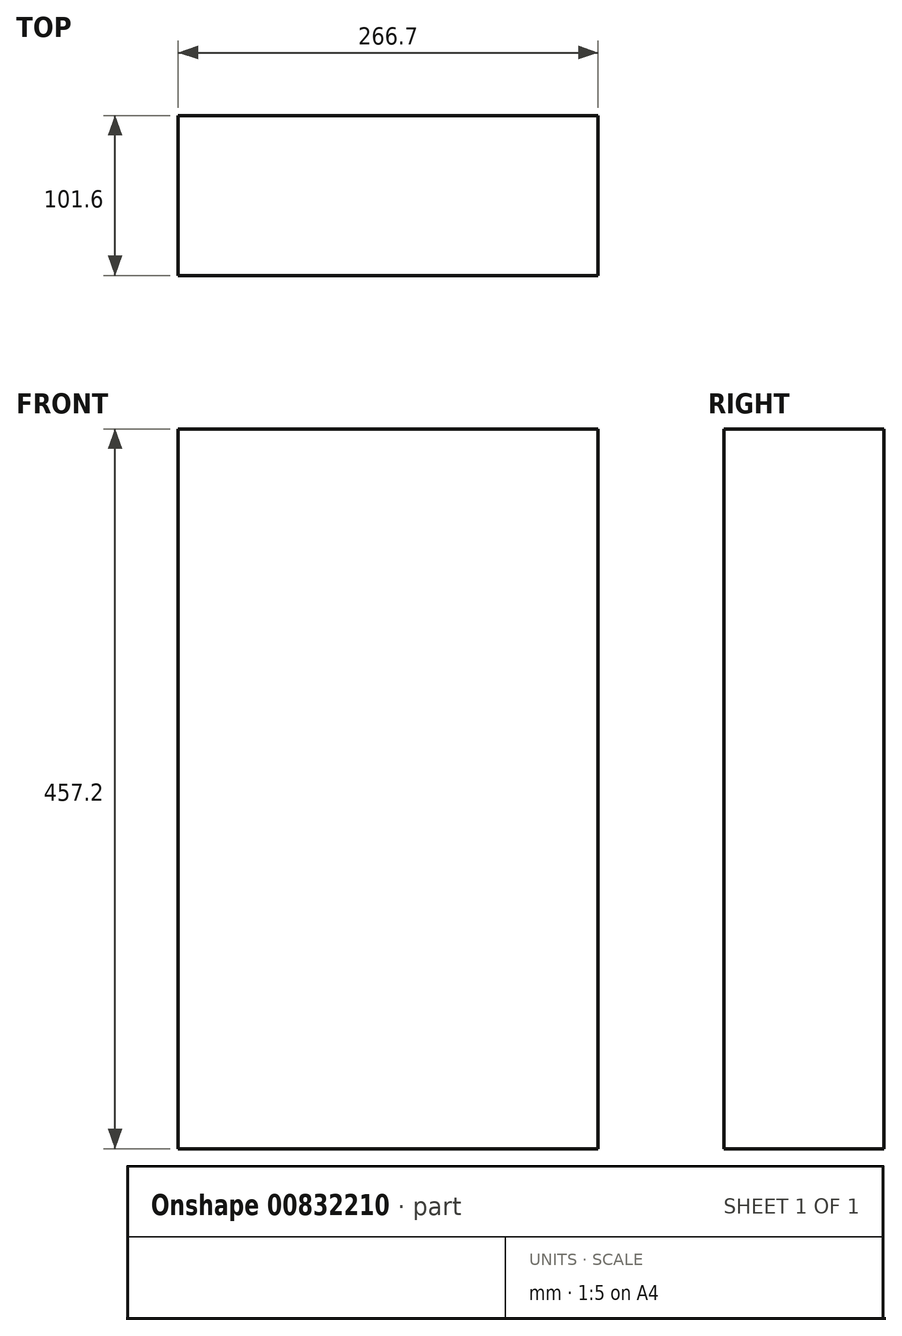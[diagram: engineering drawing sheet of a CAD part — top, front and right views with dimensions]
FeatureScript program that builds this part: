
annotation { "Feature Type Name" : "Feature", "Feature Type Description" : "" }
export const myFeature = defineFeature(function(context is Context, id is Id, definition is map)
    precondition{}
    {
        {
            var Q0;
            Q0=qCreatedBy(makeId("Front.planeOp"),FACE);
            var sketch = newSketch(context, id + "F0", { "sketchPlane" : qUnion([Q0])});
            skLineSegment(sketch, "E0.bottom", {"start": v(133.35, 228.6) * mm, "end": v(-133.35, 228.6) * mm});
            skLineSegment(sketch, "E0.top", {"start": v(133.35, -228.6) * mm, "end": v(-133.35, -228.6) * mm});
            skLineSegment(sketch, "E0.left", {"start": v(133.35, 228.6) * mm, "end": v(133.35, -228.6) * mm});
            skLineSegment(sketch, "E0.right", {"start": v(-133.35, 228.6) * mm, "end": v(-133.35, -228.6) * mm});
            skPoint(sketch, "E0.middle", {"position": v(0, 0) * mm});
            skSolve(sketch);
        }
        {
            var Q0;
            Q0=qSketchRegion(id+"F0",true);
            extrude(context, id + "F1", {"entities" : qUnion([Q0]), "depth" : 101.6 * mm, "offsetDistance" : 25.4 * mm});
        }
    });
